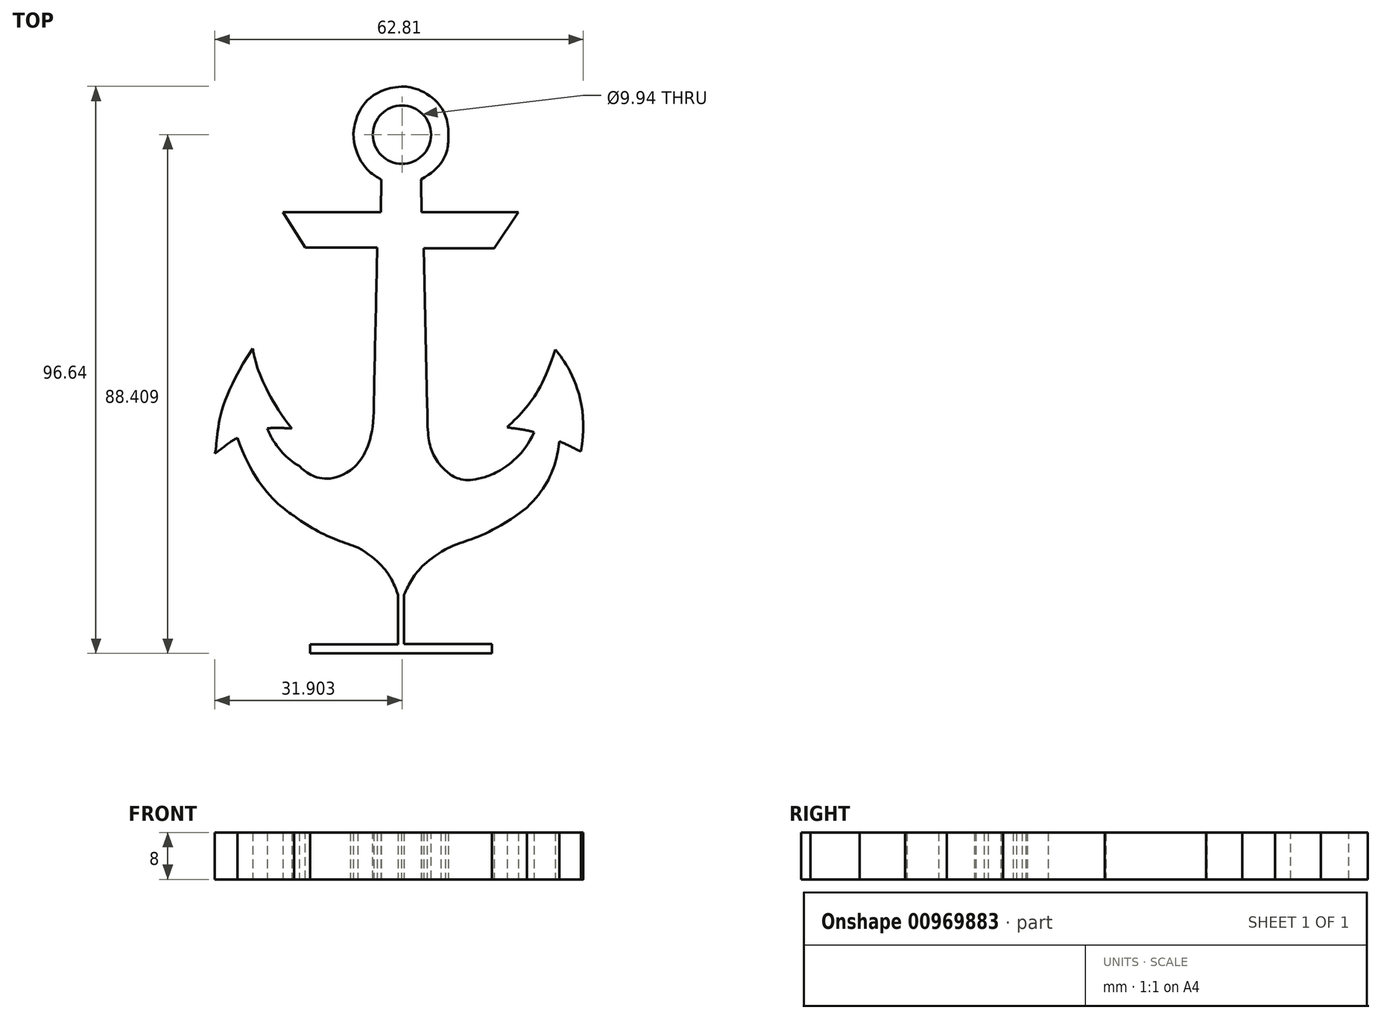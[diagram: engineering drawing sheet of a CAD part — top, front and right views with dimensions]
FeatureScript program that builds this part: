
annotation { "Feature Type Name" : "Feature", "Feature Type Description" : "" }
export const myFeature = defineFeature(function(context is Context, id is Id, definition is map)
    precondition{}
    {
        {
            var Q0;
            Q0=qCreatedBy(makeId("Top.planeOp"),FACE);
            var sketch = newSketch(context, id + "F0", { "sketchPlane" : qUnion([Q0])});
            skFitSpline(sketch, "E0", {"points": [v(6.47, 42.3) * mm, v(0, 24.38) * mm], "startDerivative": vector(-20.77, -30.94) * mm, "endDerivative": vector(-2.28, -9.13) * mm});
            skFitSpline(sketch, "E1", {"points": [v(0, 24.38) * mm, v(3.87, 27.07) * mm], "startDerivative": vector(3.87, 2.69) * mm, "endDerivative": vector(3.17, 1.31) * mm});
            skFitSpline(sketch, "E2", {"points": [v(3.87, 27.07) * mm, v(13.52, 13.76) * mm], "startDerivative": vector(8.73, -26.24) * mm, "endDerivative": vector(5.23, -3.32) * mm});
            skFitSpline(sketch, "E3", {"points": [v(13.52, 13.76) * mm, v(24.4, 8.38) * mm], "startDerivative": vector(12.55, -9.43) * mm, "endDerivative": vector(10.01, -3.48) * mm});
            skFitSpline(sketch, "E4", {"points": [v(39.3, 8.08) * mm, v(53.17, 15.17) * mm], "startDerivative": vector(9.08, 5.07) * mm, "endDerivative": vector(22.37, 17.14) * mm});
            skFitSpline(sketch, "E5", {"points": [v(53.17, 15.17) * mm, v(58.73, 26.46) * mm], "startDerivative": vector(13.27, 12.81) * mm, "endDerivative": vector(1.4, 9.74) * mm});
            skFitSpline(sketch, "E6", {"points": [v(58.73, 26.46) * mm, v(62.42, 24.77) * mm], "startDerivative": vector(4.29, -1.5) * mm, "endDerivative": vector(2.58, -0.84) * mm});
            skFitSpline(sketch, "E7", {"points": [v(62.42, 24.77) * mm, v(58.02, 42.13) * mm], "startDerivative": vector(5.37, 29.44) * mm, "endDerivative": vector(-3.81, 4.37) * mm});
            skFitSpline(sketch, "E8", {"points": [v(58.02, 42.13) * mm, v(49.82, 28.87) * mm], "startDerivative": vector(-7, -22.8) * mm, "endDerivative": vector(-9.73, -9.44) * mm});
            skFitSpline(sketch, "E9", {"points": [v(49.82, 28.87) * mm, v(54.4, 28) * mm], "startDerivative": vector(4.58, -0.88) * mm, "endDerivative": vector(3.46, -1.52) * mm});
            skFitSpline(sketch, "E10", {"points": [v(54.4, 28) * mm, v(46.08, 20.41) * mm], "startDerivative": vector(-7.36, -15.88) * mm, "endDerivative": vector(-5.31, -1.77) * mm});
            skFitSpline(sketch, "E11", {"points": [v(46.08, 20.41) * mm, v(38.5, 22.26) * mm], "startDerivative": vector(-13.44, -4.43) * mm, "endDerivative": vector(-4.45, 4.1) * mm});
            skFitSpline(sketch, "E12", {"points": [v(38.5, 22.26) * mm, v(36.2, 32.48) * mm], "startDerivative": vector(-5.87, 8.06) * mm, "endDerivative": vector(-0.05, 18.95) * mm});
            skFitSpline(sketch, "E13", {"points": [v(36.2, 32.48) * mm, v(35.64, 59.4) * mm], "startDerivative": vector(-0.57, 26.92) * mm, "endDerivative": vector(-0.57, 26.92) * mm});
            skFitSpline(sketch, "E14", {"points": [v(35.64, 59.4) * mm, v(47.62, 59.4) * mm], "startDerivative": vector(11.98, 0) * mm, "endDerivative": vector(11.98, 0) * mm});
            skFitSpline(sketch, "E15", {"points": [v(47.62, 59.4) * mm, v(51.76, 65.53) * mm], "startDerivative": vector(4.14, 6.12) * mm, "endDerivative": vector(4.14, 6.12) * mm});
            skFitSpline(sketch, "E16", {"points": [v(51.76, 65.53) * mm, v(35.24, 65.53) * mm], "startDerivative": vector(-16.52, 0) * mm, "endDerivative": vector(-16.52, 0) * mm});
            skFitSpline(sketch, "E17", {"points": [v(35.24, 65.53) * mm, v(35.14, 71.13) * mm], "startDerivative": vector(0, 5.55) * mm, "endDerivative": vector(0, 5.55) * mm});
            skFitSpline(sketch, "E18", {"points": [v(35.14, 71.13) * mm, v(39.82, 78.92) * mm], "startDerivative": vector(15.73, 8.02) * mm, "endDerivative": vector(0.23, 3.6) * mm});
            skFitSpline(sketch, "E19", {"points": [v(39.82, 78.92) * mm, v(31.8, 86.94) * mm], "startDerivative": vector(0.17, 20) * mm, "endDerivative": vector(-4.4, -0.78) * mm});
            skFitSpline(sketch, "E20", {"points": [v(31.8, 86.94) * mm, v(23.6, 78.92) * mm], "startDerivative": vector(-23.75, -1.8) * mm, "endDerivative": vector(-0.46, -2.43) * mm});
            skFitSpline(sketch, "E21", {"points": [v(23.6, 78.92) * mm, v(28.35, 71.1) * mm], "startDerivative": vector(0.82, -17.41) * mm, "endDerivative": vector(1.87, -1.12) * mm});
            skFitSpline(sketch, "E22", {"points": [v(28.35, 71.1) * mm, v(28.32, 65.53) * mm], "startDerivative": vector(0, -5.55) * mm, "endDerivative": vector(0, -5.55) * mm});
            skFitSpline(sketch, "E23", {"points": [v(28.32, 65.53) * mm, v(11.58, 65.53) * mm], "startDerivative": vector(-16.74, 0) * mm, "endDerivative": vector(-16.74, 0) * mm});
            skFitSpline(sketch, "E24", {"points": [v(11.58, 65.53) * mm, v(15.4, 59.52) * mm], "startDerivative": vector(3.66, -5.73) * mm, "endDerivative": vector(3.66, -5.73) * mm});
            skFitSpline(sketch, "E25", {"points": [v(15.4, 59.52) * mm, v(27.68, 59.47) * mm], "startDerivative": vector(12.34, -0.4) * mm, "endDerivative": vector(12.34, -0.4) * mm});
            skFitSpline(sketch, "E26", {"points": [v(27.68, 59.47) * mm, v(27.09, 32.48) * mm], "startDerivative": vector(-0.48, -26.92) * mm, "endDerivative": vector(-0.48, -26.92) * mm});
            skFitSpline(sketch, "E27", {"points": [v(27.09, 32.48) * mm, v(23.08, 21.56) * mm], "startDerivative": vector(0.51, -22.68) * mm, "endDerivative": vector(-2.7, -1.52) * mm});
            skFitSpline(sketch, "E28", {"points": [v(23.08, 21.56) * mm, v(14.4, 22.26) * mm], "startDerivative": vector(-14.23, -9.92) * mm, "endDerivative": vector(-2.2, 2.1) * mm});
            skFitSpline(sketch, "E29", {"points": [v(14.4, 22.26) * mm, v(8.96, 28.66) * mm], "startDerivative": vector(-9.56, 5.37) * mm, "endDerivative": vector(-1.28, 4.05) * mm});
            skFitSpline(sketch, "E30", {"points": [v(8.96, 28.66) * mm, v(13.15, 28.66) * mm], "startDerivative": vector(2.14, 0.56) * mm, "endDerivative": vector(4.2, -0.33) * mm});
            skFitSpline(sketch, "E31", {"points": [v(6.47, 42.3) * mm, v(13.15, 28.66) * mm], "startDerivative": vector(0.65, -5.92) * mm, "endDerivative": vector(14.86, -18.43) * mm});
            skFitSpline(sketch, "E32", {"points": [v(24.4, 8.38) * mm, v(31.23, 0.33) * mm], "startDerivative": vector(15.77, -9.5) * mm, "endDerivative": vector(2.65, -6.84) * mm});
            skFitSpline(sketch, "E33", {"points": [v(31.23, 0.33) * mm, v(32.24, 0.33) * mm], "startDerivative": vector(1.02, 0) * mm, "endDerivative": vector(1.02, 0) * mm});
            skFitSpline(sketch, "E34", {"points": [v(39.3, 8.08) * mm, v(32.24, 0.33) * mm], "startDerivative": vector(-15.34, -9.37) * mm, "endDerivative": vector(-4.15, -8.26) * mm});
            skSolve(sketch);
        }
        {
            var Q0;
            Q0 = qSketchRegion(id + "F0", true);
            extrude(context, id + "F1", {"entities" : qUnion([Q0]), "depth" : 8 * mm, "offsetDistance" : 25.4 * mm});
        }
        {
            var Q0;
            Q0=makeQuery(id+"F1.opExtrude","CAP_FACE",FACE,{"disambiguationData":[OSD([sQuery(id+"F0.wireOp",EDGE,"E0"),sQuery(id+"F0.wireOp",EDGE,"E1"),sQuery(id+"F0.wireOp",EDGE,"E2"),sQuery(id+"F0.wireOp",EDGE,"E3"),sQuery(id+"F0.wireOp",EDGE,"762db188-21d7-43b6-ae56-59e89dc9cb7d"),sQuery(id+"F0.wireOp",EDGE,"154abf6c-8d95-44e8-b5e1-2564ad344a1f"),sQuery(id+"F0.wireOp",EDGE,"E4"),sQuery(id+"F0.wireOp",EDGE,"E5"),sQuery(id+"F0.wireOp",EDGE,"E6"),sQuery(id+"F0.wireOp",EDGE,"E7"),sQuery(id+"F0.wireOp",EDGE,"E8"),sQuery(id+"F0.wireOp",EDGE,"E9"),sQuery(id+"F0.wireOp",EDGE,"E10"),sQuery(id+"F0.wireOp",EDGE,"E11"),sQuery(id+"F0.wireOp",EDGE,"E12"),sQuery(id+"F0.wireOp",EDGE,"E13"),sQuery(id+"F0.wireOp",EDGE,"E14"),sQuery(id+"F0.wireOp",EDGE,"E15"),sQuery(id+"F0.wireOp",EDGE,"E16"),sQuery(id+"F0.wireOp",EDGE,"E17"),sQuery(id+"F0.wireOp",EDGE,"E18"),sQuery(id+"F0.wireOp",EDGE,"E19"),sQuery(id+"F0.wireOp",EDGE,"E20"),sQuery(id+"F0.wireOp",EDGE,"E21"),sQuery(id+"F0.wireOp",EDGE,"E22"),sQuery(id+"F0.wireOp",EDGE,"E23"),sQuery(id+"F0.wireOp",EDGE,"E24"),sQuery(id+"F0.wireOp",EDGE,"E25"),sQuery(id+"F0.wireOp",EDGE,"E26"),sQuery(id+"F0.wireOp",EDGE,"E27"),sQuery(id+"F0.wireOp",EDGE,"E28"),sQuery(id+"F0.wireOp",EDGE,"E29"),sQuery(id+"F0.wireOp",EDGE,"E30"),sQuery(id+"F0.wireOp",EDGE,"E31")])],"isStart":false});
            var sketch = newSketch(context, id + "F2", { "sketchPlane" : qUnion([Q0])});
            skCircle(sketch, "E35", {"center": v(31.9, 78.74) * mm, "radius": 4.97 * mm});
            skSolve(sketch);
        }
        {
            var Q0;
            Q0=makeQuery(id+"F2.imprint","IMPRINT",FACE,{"disambiguationData":[TD([[makeQuery(id+"F2.imprint","IMPRINT",EDGE,{"derivedFrom":sQuery(id+"F2.wireOp",EDGE,"E35")}),1.0]])]});
            var Q1;
            Q1=sQuery(id+"F2.wireOp",EDGE,"E35");
            extrude(context, id + "F3", {"entities" : qUnion([Q0]), "operationType" : NewBodyOperationType.REMOVE, "surfaceEntities" : qUnion([Q1]), "oppositeDirection" : true, "depth" : 8 * mm, "offsetDistance" : 25 * mm});
        }
        {
            var Q0;
            Q0=makeQuery(id+"F1.opExtrude","SWEPT_FACE",FACE,{"disambiguationData":[OSD([sQuery(id+"F0.wireOp",EDGE,"E33")])]});
            extrude(context, id + "F4", {"entities" : qUnion([Q0]), "operationType" : NewBodyOperationType.ADD, "depth" : 10 * mm, "offsetDistance" : 25 * mm});
        }
        {
            var Q0;
            Q0=makeQuery(id+"F4.opExtrude","SWEPT_FACE",FACE,{"disambiguationData":[OSD([sQuery(id+"F0.wireOp",EDGE,"E33"),sQuery(id+"F0.wireOp",EDGE,"E34")])]});
            var sketch = newSketch(context, id + "F5", { "sketchPlane" : qUnion([Q0])});
            skLineSegment(sketch, "E36", {"start": v(-9.67, 8) * mm, "end": v(-9.67, 0) * mm});
            skLineSegment(sketch, "E37", {"start": v(-9.67, 0) * mm, "end": v(-8.04, 0) * mm});
            skLineSegment(sketch, "E38", {"start": v(-8.04, 0) * mm, "end": v(-8.04, 8) * mm});
            skLineSegment(sketch, "E39", {"start": v(-8.04, 8) * mm, "end": v(-9.67, 8) * mm});
            skSolve(sketch);
        }
        {
            var Q0;
            Q0=makeQuery(id+"F5.imprint","IMPRINT",FACE,{"disambiguationData":[TD([[makeQuery(id+"F5.imprint","IMPRINT",EDGE,{"derivedFrom":sQuery(id+"F5.wireOp",EDGE,"E36")}),1.0]])]});
            extrude(context, id + "F6", {"entities" : qUnion([Q0]), "operationType" : NewBodyOperationType.ADD, "depth" : 15 * mm, "offsetDistance" : 25 * mm});
        }
        {
            var Q0;
            Q0=makeQuery(id+"F4.opExtrude","SWEPT_FACE",FACE,{"disambiguationData":[OSD([sQuery(id+"F0.wireOp",EDGE,"E32"),sQuery(id+"F0.wireOp",EDGE,"E33")])]});
            var sketch = newSketch(context, id + "F7", { "sketchPlane" : qUnion([Q0])});
            skLineSegment(sketch, "E40", {"start": v(9.67, 0) * mm, "end": v(9.67, 8) * mm});
            skLineSegment(sketch, "E41", {"start": v(9.67, 8) * mm, "end": v(8.1, 8) * mm});
            skLineSegment(sketch, "E42", {"start": v(8.1, 8) * mm, "end": v(8.1, 0) * mm});
            skLineSegment(sketch, "E43", {"start": v(8.1, 0) * mm, "end": v(9.67, 0) * mm});
            skSolve(sketch);
        }
        {
            var Q0;
            Q0=makeQuery(id+"F7.imprint","IMPRINT",FACE,{"disambiguationData":[TD([[makeQuery(id+"F7.imprint","IMPRINT",EDGE,{"derivedFrom":sQuery(id+"F7.wireOp",EDGE,"E40")}),-1.0]])]});
            extrude(context, id + "F8", {"entities" : qUnion([Q0]), "operationType" : NewBodyOperationType.ADD, "depth" : 15 * mm, "offsetDistance" : 25 * mm});
        }
    });
